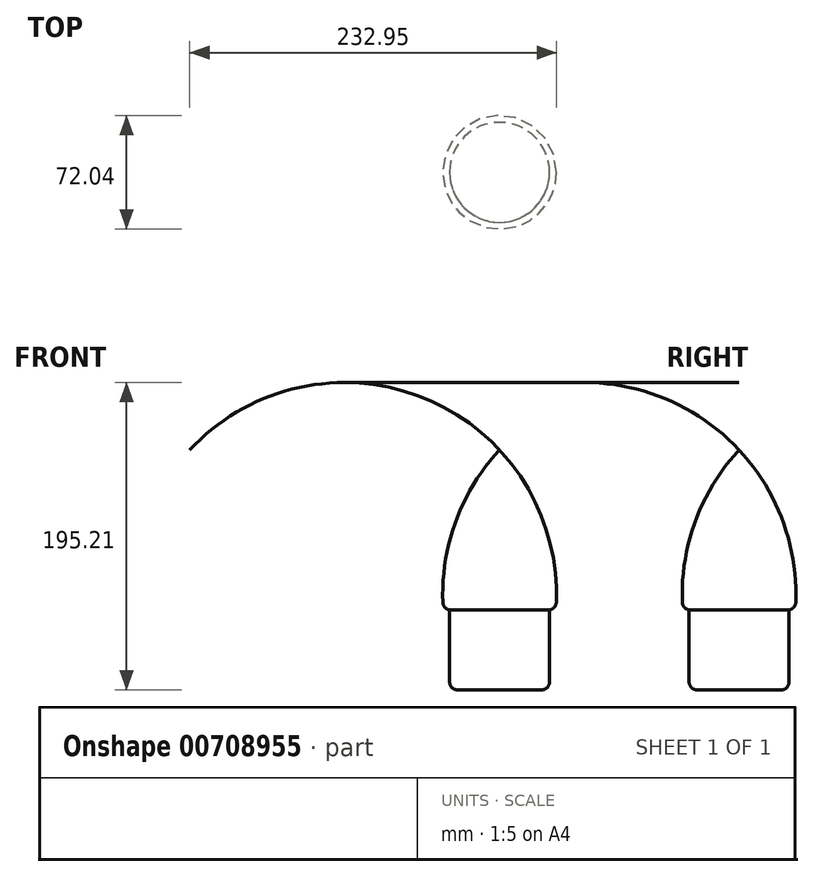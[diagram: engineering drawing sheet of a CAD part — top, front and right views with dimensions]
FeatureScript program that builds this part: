
annotation { "Feature Type Name" : "Feature", "Feature Type Description" : "" }
export const myFeature = defineFeature(function(context is Context, id is Id, definition is map)
    precondition{}
    {
        {
            var Q0;
            Q0=qCreatedBy(makeId("Right.planeOp"),FACE);
            var sketch = newSketch(context, id + "F0", { "sketchPlane" : qUnion([Q0])});
            skLineSegment(sketch, "E0", {"start": v(0, 0) * mm, "end": v(-31.75, 0) * mm});
            skLineSegment(sketch, "E1", {"start": v(-31.75, 0) * mm, "end": v(-31.75, 50.8) * mm});
            skLineSegment(sketch, "E2", {"start": v(0, 0) * mm, "end": v(0, 152.4) * mm});
            skLineSegment(sketch, "E3", {"start": v(-31.75, 50.8) * mm, "end": v(-35.75, 50.8) * mm});
            skArc(sketch, "E4", {"start": v(0, 152.4) * mm, "mid": v(-28.49, 105.33) * mm, "end": v(-35.75, 50.8) * mm});
            skLineSegment(sketch, "E5", {"start": v(0, 152.4) * mm, "end": v(0, 0) * mm, "construction": true});
            skSolve(sketch);
        }
        {
            var Q0;
            Q0=makeQuery(id+"F0.imprint","IMPRINT",FACE,{"disambiguationData":[TD([[makeQuery(id+"F0.imprint","IMPRINT",EDGE,{"derivedFrom":sQuery(id+"F0.wireOp",EDGE,"E0")}),-1.0]])]});
            var Q1;
            Q1=sQuery(id+"F0.wireOp",EDGE,"E2");
            revolve(context, id + "F1", {"surfaceOperationType" : NewSurfaceOperationType.NEW, "entities" : qUnion([Q0]), "axis" : qUnion([Q1]), "revolveType" : RevolveType.FULL});
        }
        {
            var Q0;
            Q0=makeQuery(id+"F1.opRevolve","SWEPT_EDGE",EDGE,{"disambiguationData":[OSD([sQuery(id+"F0.wireOp",EDGE,"E3"),sQuery(id+"F0.wireOp",EDGE,"E4")])]});
            var Q1;
            Q1=makeQuery(id+"F1.opRevolve","SWEPT_EDGE",EDGE,{"disambiguationData":[OSD([sQuery(id+"F0.wireOp",EDGE,"E0"),sQuery(id+"F0.wireOp",EDGE,"E1")])]});
            fillet(context, id + "F2", {"entities" : qUnion([Q0, Q1]), "radius" : 5.08 * mm, "tangentPropagation" : true, "allowEdgeOverflow" : false});
        }
    });
